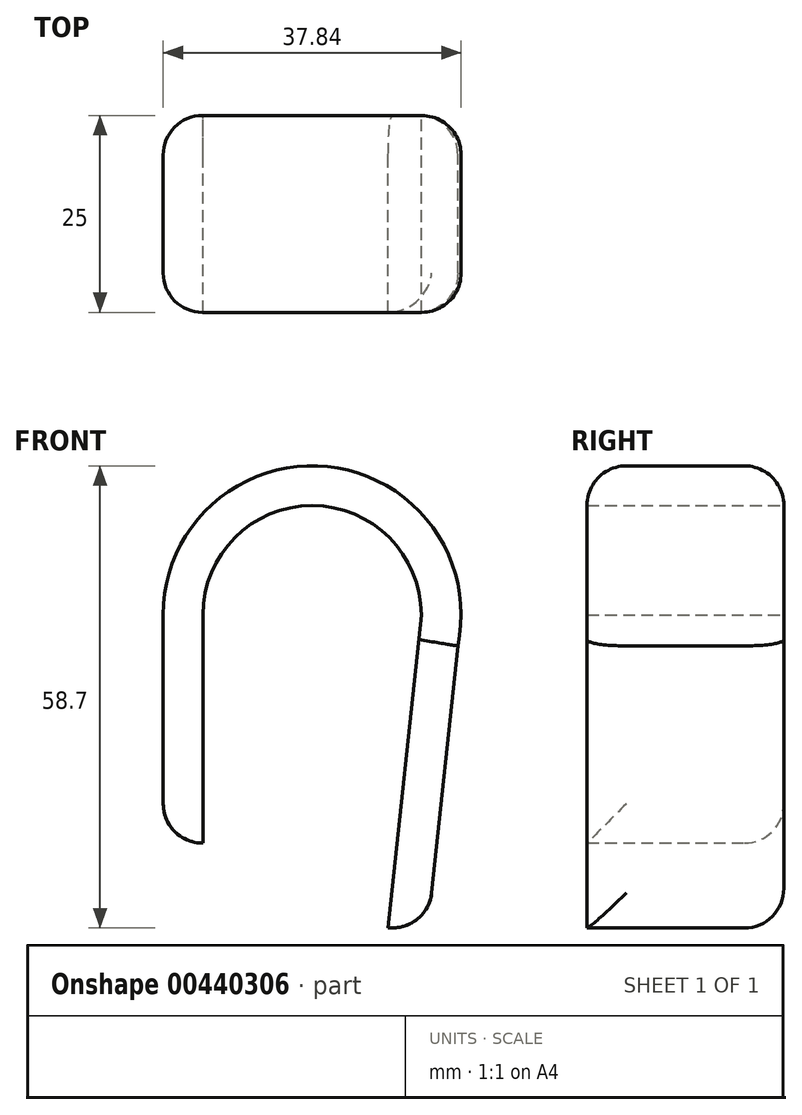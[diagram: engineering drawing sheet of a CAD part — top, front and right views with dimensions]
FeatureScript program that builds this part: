
annotation { "Feature Type Name" : "Feature", "Feature Type Description" : "" }
export const myFeature = defineFeature(function(context is Context, id is Id, definition is map)
    precondition{}
    {
        {
            var Q0;
            Q0=qCreatedBy(makeId("Front.planeOp"),FACE);
            var sketch = newSketch(context, id + "F0", { "sketchPlane" : qUnion([Q0])});
            skArc(sketch, "E0", {"start": v(18.5, -3.95) * mm, "mid": v(1.99, 18.82) * mm, "end": v(-18.92, 0) * mm});
            skArc(sketch, "E1", {"start": v(13.57, -2.9) * mm, "mid": v(1.46, 13.8) * mm, "end": v(-13.87, 0) * mm});
            skLineSegment(sketch, "E2", {"start": v(-18.92, 0) * mm, "end": v(-18.92, -29) * mm});
            skLineSegment(sketch, "E3", {"start": v(-13.87, 0) * mm, "end": v(-13.87, -29) * mm});
            skLineSegment(sketch, "E4", {"start": v(13.87, 0) * mm, "end": v(9.67, -39.78) * mm});
            skLineSegment(sketch, "E5", {"start": v(18.92, 0) * mm, "end": v(14.72, -39.78) * mm});
            skLineSegment(sketch, "E6", {"start": v(-18.92, -29) * mm, "end": v(-13.87, -29) * mm});
            skLineSegment(sketch, "E7", {"start": v(9.67, -39.78) * mm, "end": v(14.72, -39.78) * mm});
            skSolve(sketch);
        }
        {
            var Q0;
            Q0 = qSketchRegion(id + "F0", true);
            extrude(context, id + "F1", {"entities" : qUnion([Q0]), "depth" : 25 * mm});
        }
        {
            var Q0;
            Q0=makeQuery(id+"F1.opExtrude","CAP_EDGE",EDGE,{"disambiguationData":[OSD([sQuery(id+"F0.wireOp",EDGE,"E5")])],"isStart":true});
            var Q1;
            Q1=makeQuery(id+"F1.opExtrude","CAP_EDGE",EDGE,{"disambiguationData":[OSD([sQuery(id+"F0.wireOp",EDGE,"E0")])],"isStart":true});
            fillet(context, id + "F2", {"entities" : qUnion([Q0, Q1]), "radius" : 5 * mm, "tangentPropagation" : true, "allowEdgeOverflow" : false});
        }
        {
            var Q0;
            Q0=makeQuery(id+"F1.opExtrude","SWEPT_EDGE",EDGE,{"disambiguationData":[OSD([sQuery(id+"F0.wireOp",EDGE,"E5"),sQuery(id+"F0.wireOp",EDGE,"E7")])]});
            var Q1;
            Q1=makeQuery(id+"F1.opExtrude","CAP_EDGE",EDGE,{"disambiguationData":[OSD([sQuery(id+"F0.wireOp",EDGE,"E5")])],"isStart":false});
            var Q2;
            Q2=makeQuery(id+"F1.opExtrude","CAP_EDGE",EDGE,{"disambiguationData":[OSD([sQuery(id+"F0.wireOp",EDGE,"E0")])],"isStart":false});
            var Q3;
            Q3=makeQuery(id+"F1.opExtrude","SWEPT_EDGE",EDGE,{"disambiguationData":[OSD([sQuery(id+"F0.wireOp",EDGE,"E2"),sQuery(id+"F0.wireOp",EDGE,"E6")])]});
            fillet(context, id + "F3", {"entities" : qUnion([Q0, Q1, Q2, Q3]), "radius" : 5 * mm, "tangentPropagation" : true, "allowEdgeOverflow" : false});
        }
    });
